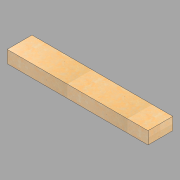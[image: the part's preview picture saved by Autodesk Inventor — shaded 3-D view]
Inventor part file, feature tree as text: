
AUTODESK INVENTOR PART (.ipt)
format: ipt  version: 2022.1 (Build 261234020, 234B)  size: 101,888 bytes
history: native  units: in
note: dims shown in document units (in); Inventor stores cm internally (conversion verified against a paired STEP export)
features: extrude x1, sketch x1
ambient origin geometry x8: Origin, YZ Plane, XZ Plane, XY Plane, X Axis, Y Axis, Z Axis, Center Point
bodies: Solid1 (feature_tree)
feature tree (2):
  extrude  "Extrusion1"  Depth=12.0in
  sketch  "Sketch1"  dims[d0=6.0in d1=12.0in d2=68.125in d3=0.0in]
